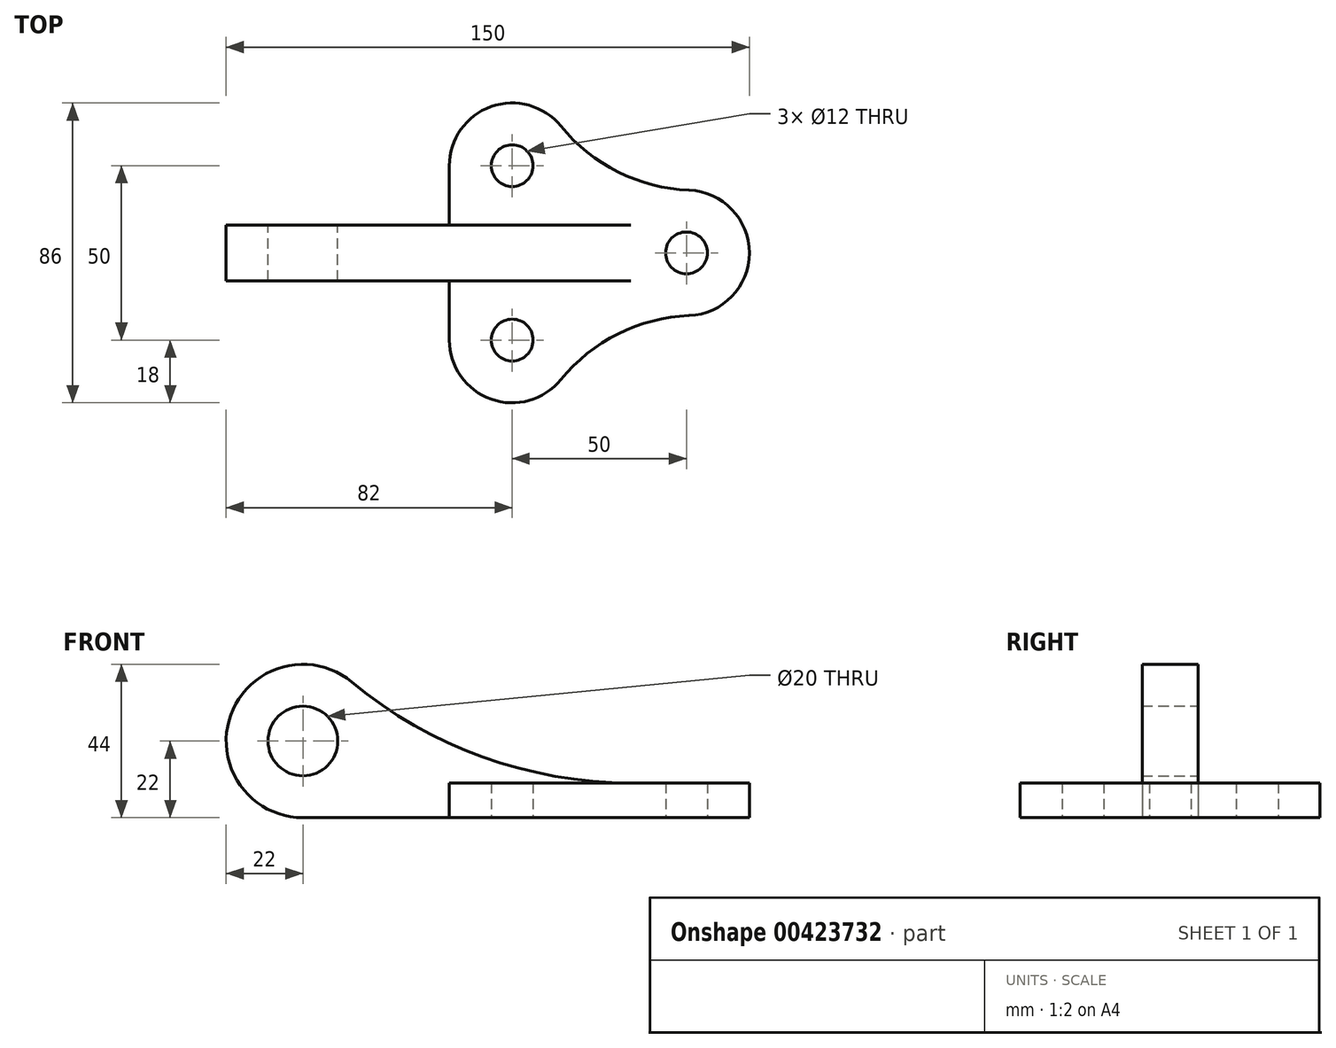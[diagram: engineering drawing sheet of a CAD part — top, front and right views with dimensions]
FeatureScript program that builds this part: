
annotation { "Feature Type Name" : "Feature", "Feature Type Description" : "" }
export const myFeature = defineFeature(function(context is Context, id is Id, definition is map)
    precondition{}
    {
        {
            var Q0;
            Q0=qCreatedBy(makeId("Top.planeOp"),FACE);
            var sketch = newSketch(context, id + "F0", { "sketchPlane" : qUnion([Q0])});
            skArc(sketch, "E0", {"start": v(13.96, 36.37) * mm, "mid": v(-6.03, 41.96) * mm, "end": v(-18, 25) * mm});
            skArc(sketch, "E1", {"start": v(-18, -25) * mm, "mid": v(-6.03, -41.96) * mm, "end": v(13.96, -36.37) * mm});
            skLineSegment(sketch, "E2", {"start": v(0, 25) * mm, "end": v(0, -25) * mm, "construction": true});
            skArc(sketch, "E3", {"start": v(50.72, -17.99) * mm, "mid": v(68, 0) * mm, "end": v(50.72, 17.99) * mm});
            skArc(sketch, "E4", {"start": v(13.96, 36.37) * mm, "mid": v(30.36, 23.22) * mm, "end": v(50.72, 17.99) * mm});
            skArc(sketch, "E5.MirrorCS", {"start": v(13.96, -36.37) * mm, "mid": v(30.36, -23.22) * mm, "end": v(50.72, -17.99) * mm});
            skLineSegment(sketch, "E6", {"start": v(-18, 25) * mm, "end": v(-18, -25) * mm});
            skCircle(sketch, "E7", {"center": v(0, 25) * mm, "radius": 6 * mm});
            skCircle(sketch, "E8", {"center": v(50, 0) * mm, "radius": 6 * mm});
            skCircle(sketch, "E9", {"center": v(0, -25) * mm, "radius": 6 * mm});
            skSolve(sketch);
        }
        {
            var Q0;
            Q0=makeQuery(id+"F0.imprint","IMPRINT",FACE,{"disambiguationData":[TD([[makeQuery(id+"F0.imprint","IMPRINT",EDGE,{"derivedFrom":sQuery(id+"F0.wireOp",EDGE,"E0")}),1.0]])]});
            extrude(context, id + "F1", {"entities" : qUnion([Q0]), "depth" : 10 * mm});
        }
        {
            var Q0;
            Q0=qCreatedBy(makeId("Front.planeOp"),FACE);
            var sketch = newSketch(context, id + "F2", { "sketchPlane" : qUnion([Q0])});
            skArc(sketch, "E10", {"start": v(-45.93, 38.91) * mm, "mid": v(-80.69, 29.48) * mm, "end": v(-60, 0) * mm});
            skLineSegment(sketch, "E11.0", {"start": v(13.96, 10) * mm, "end": v(50.72, 10) * mm, "construction": true});
            skArc(sketch, "E12", {"start": v(-45.93, 38.91) * mm, "mid": v(-8.49, 17.45) * mm, "end": v(34.02, 10) * mm});
            skLineSegment(sketch, "E13", {"start": v(0, 0) * mm, "end": v(-60, 0) * mm});
            skLineSegment(sketch, "E14", {"start": v(34.02, 10) * mm, "end": v(34.02, 0) * mm});
            skLineSegment(sketch, "E15", {"start": v(34.02, 0) * mm, "end": v(0, 0) * mm});
            skLineSegment(sketch, "E16.0", {"start": v(44, 10) * mm, "end": v(56, 10) * mm});
            skLineSegment(sketch, "E17", {"start": v(50, 10) * mm, "end": v(50, 37.7) * mm, "construction": true});
            skCircle(sketch, "E18", {"center": v(-60, 22) * mm, "radius": 10 * mm});
            skSolve(sketch);
        }
        {
            var Q0;
            Q0=makeQuery(id+"F2.imprint","IMPRINT",FACE,{"disambiguationData":[TD([[makeQuery(id+"F2.imprint","IMPRINT",EDGE,{"derivedFrom":sQuery(id+"F2.wireOp",EDGE,"E10")}),1.0]])]});
            extrude(context, id + "F3", {"entities" : qUnion([Q0]), "operationType" : NewBodyOperationType.ADD, "endBound" : BoundingType.SYMMETRIC, "depth" : 16 * mm});
        }
    });
